# Revit family: Air_Purification-Panel-Armstrong-Sincerus
name_source: partatom
category: Specialty Equipment
units: mm (PartAtom-declared; Revit-internal decimal feet)

## family parameters
Cut with Voids When Loaded = No
Host = Face
OmniClass Number = 23.25.40.14
OmniClass Title = Demountable Partitions
Part Type = Normal
Room Calculation Point = No
Round Connector Dimension = Use Diameter
Shared = No

## types (1)
- Drywall/AcoustiBuilt Trim Kit
    Apparent Load = 0 VA
    Assembly Code = C1010200
    Brochure URL = Consult Manufacturer Website for More Information
    C LED Light = No
    C Void Length = 95 3/4"
    C Void Width = 5 3/4"
    Constraints = 1
    Default Elevation = 0"
    Description = Air Purification System
    Frequency = 60 Hz
    Height = 6 13/16"
    Installation URL = Consult Manufacturer Website for More Information
    Keynote = 10 22 19
    Length = 95 3/4"
    MSDS URL = Consult Manufacturer Website for More Information
    Maintenance URL = Consult Manufacturer Website for More Information
    Manufacturer = Armstrong Ceilings
    Manufacturer Fax Number = 1 800-572-TECH
    Model = Consult Manufacturer Website for More Information
    Number of Poles = 1
    Panel Finish = ACT - Armstrong Ceilings - ULTIMA Health Zone - Mineral Fiber - White
    Power Factor = 0
    Product Documentation Link = Consult Manufacturer Website for More Information
    Product Name = Sincerus Air Purification System
    Product Page URL = Consult Manufacturer Website for More Information
    Product Specification URL = Consult Manufacturer Website for More Information
    URL = https://www.armstrongceilings.com
    Version = 2020 - v1.0a
    Voltage = 277 V
    Warranty URL = Consult Manufacturer Website for More Information
    Width = 5 3/4"

## geometry (parser evidence)
native form markers: Sweep x13
no freeform markers — native parametric forms only
